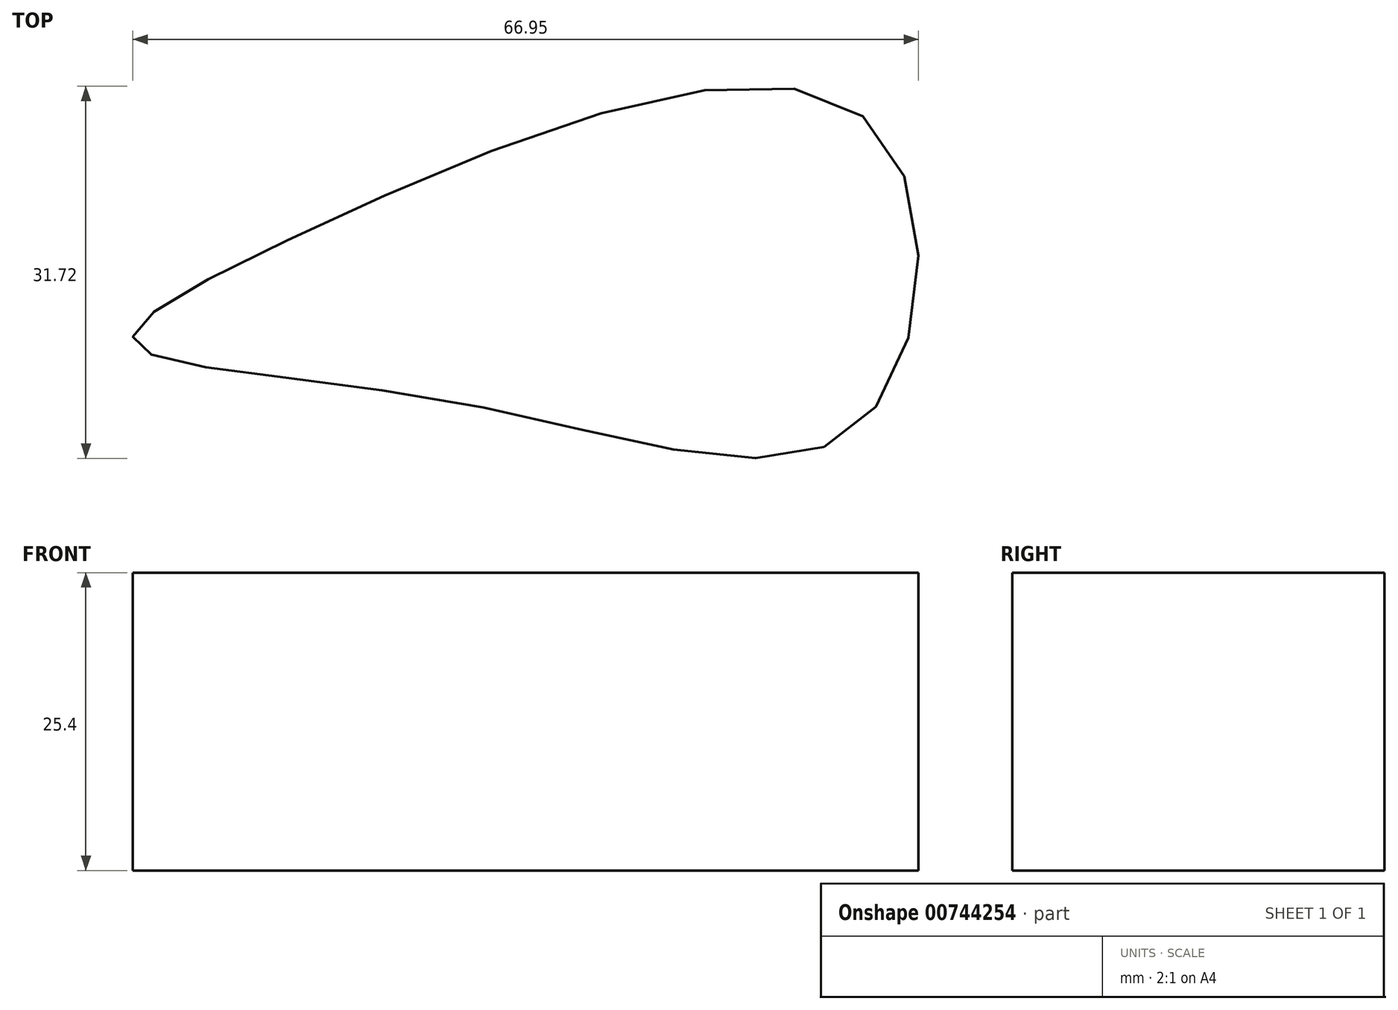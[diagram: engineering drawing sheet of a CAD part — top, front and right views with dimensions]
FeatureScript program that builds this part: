
annotation { "Feature Type Name" : "Feature", "Feature Type Description" : "" }
export const myFeature = defineFeature(function(context is Context, id is Id, definition is map)
    precondition{}
    {
        {
            var Q0;
            Q0=qCreatedBy(makeId("Top.planeOp"),FACE);
            var sketch = newSketch(context, id + "F0", { "sketchPlane" : qUnion([Q0])});
            skFitSpline(sketch, "E0", {"points": [v(0, 31.18) * mm, v(-48.34, 20.95) * mm, v(-62.1, 11.84) * mm, v(-33.96, 6.68) * mm, v(0, 5.16) * mm, v(0, 31.18) * mm]});
            skSolve(sketch);
        }
        {
            var Q0;
            Q0=makeQuery(id+"F0.imprint","IMPRINT",FACE,{"disambiguationData":[TD([[makeQuery(id+"F0.imprint","IMPRINT",EDGE,{"derivedFrom":sQuery(id+"F0.wireOp",EDGE,"E0")}),1.0]])]});
            extrude(context, id + "F1", {"entities" : qUnion([Q0]), "depth" : 25.4 * mm, "offsetDistance" : 25.4 * mm});
        }
    });
